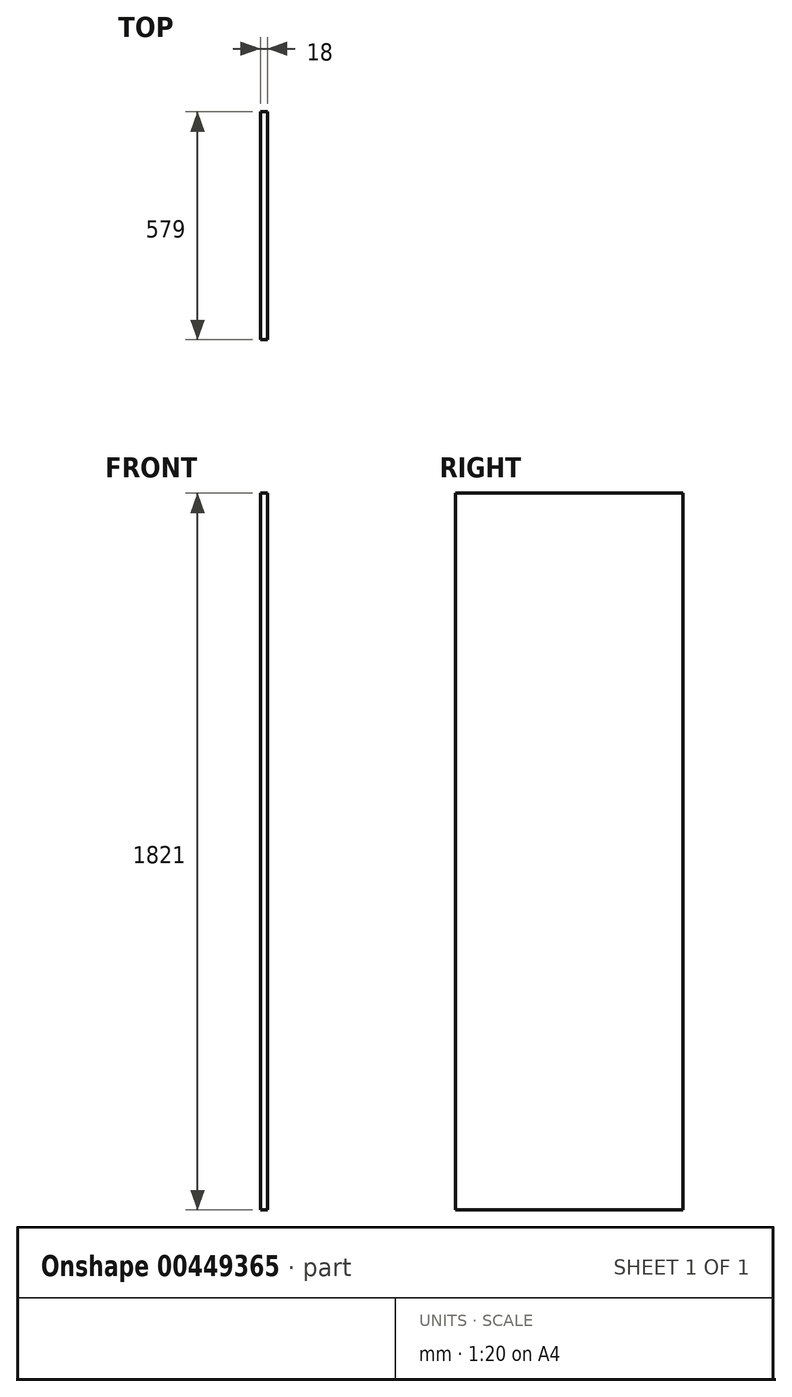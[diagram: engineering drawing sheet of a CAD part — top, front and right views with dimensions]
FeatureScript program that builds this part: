
annotation { "Feature Type Name" : "Feature", "Feature Type Description" : "" }
export const myFeature = defineFeature(function(context is Context, id is Id, definition is map)
    precondition{}
    {
        {
            var Q0;
            Q0=qCreatedBy(makeId("Right.planeOp"),FACE);
            var sketch = newSketch(context, id + "F0", { "sketchPlane" : qUnion([Q0])});
            skLineSegment(sketch, "E0.bottom", {"start": v(0, 1921) * mm, "end": v(579, 1921) * mm});
            skLineSegment(sketch, "E0.top", {"start": v(0, 100) * mm, "end": v(579, 100) * mm});
            skLineSegment(sketch, "E0.left", {"start": v(0, 1921) * mm, "end": v(0, 100) * mm});
            skLineSegment(sketch, "E0.right", {"start": v(579, 1921) * mm, "end": v(579, 100) * mm});
            skSolve(sketch);
        }
        {
            var Q0;
            Q0=qSketchRegion(id+"F0",true);
            extrude(context, id + "F1", {"entities" : qUnion([Q0]), "oppositeDirection" : true, "depth" : 18 * mm});
        }
    });
